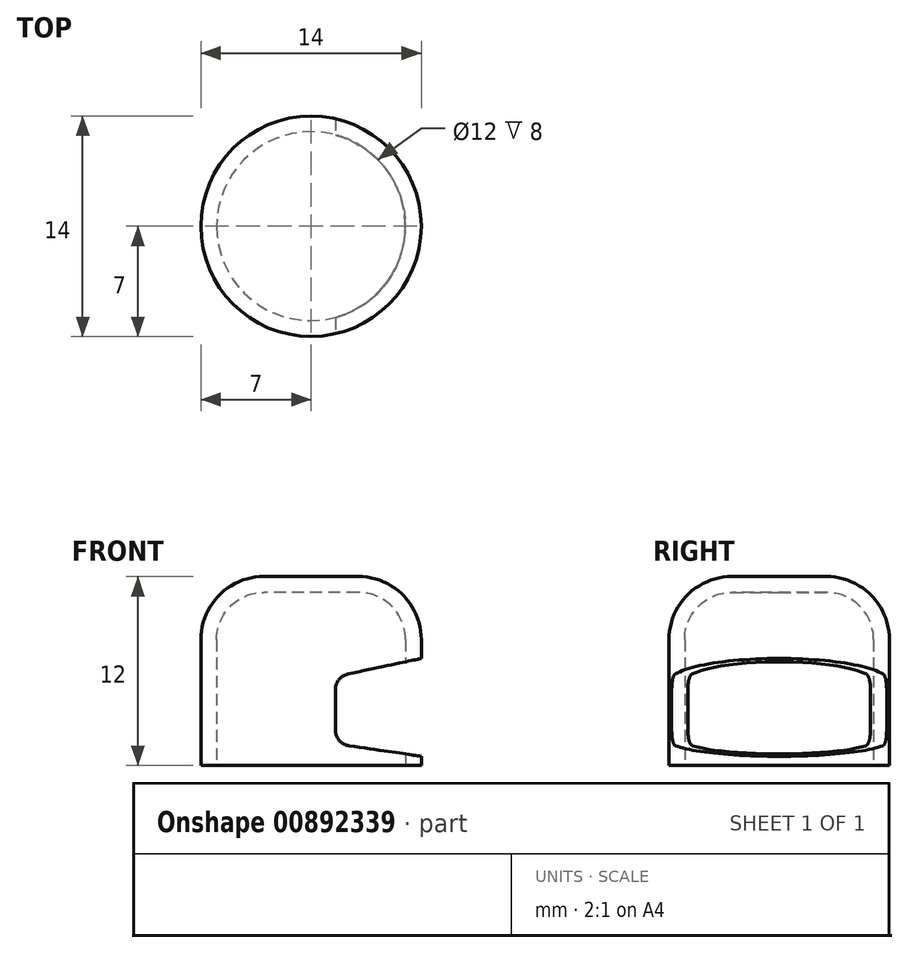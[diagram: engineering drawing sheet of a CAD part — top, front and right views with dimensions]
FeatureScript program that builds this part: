
annotation { "Feature Type Name" : "Feature", "Feature Type Description" : "" }
export const myFeature = defineFeature(function(context is Context, id is Id, definition is map)
    precondition{}
    {
        {
            var Q0;
            Q0=qCreatedBy(makeId("Top.planeOp"),FACE);
            var sketch = newSketch(context, id + "F0", { "sketchPlane" : qUnion([Q0])});
            skCircle(sketch, "E0", {"center": v(0, 0) * mm, "radius": 7 * mm});
            skSolve(sketch);
        }
        {
            var Q0;
            Q0 = qSketchRegion(id + "F0", true);
            extrude(context, id + "F1", {"entities" : qUnion([Q0]), "depth" : 12 * mm, "offsetDistance" : 25.4 * mm});
        }
        {
            var Q0;
            Q0=makeQuery(id+"F1.opExtrude","CAP_FACE",FACE,{"disambiguationData":[OSD([sQuery(id+"F0.wireOp",EDGE,"E0")])],"isStart":false});
            fillet(context, id + "F2", {"entities" : qUnion([Q0]), "radius" : 4 * mm, "tangentPropagation" : true, "allowEdgeOverflow" : false});
        }
        {
            var Q0;
            Q0=makeQuery(id+"F1.opExtrude","CAP_FACE",FACE,{"disambiguationData":[OSD([sQuery(id+"F0.wireOp",EDGE,"E0")])],"isStart":true});
            shell(context, id + "F3", {"entities" : qUnion([Q0]), "thickness" : 1 * mm});
        }
        {
            var Q0;
            Q0=qCreatedBy(makeId("Front.planeOp"),FACE);
            var sketch = newSketch(context, id + "F4", { "sketchPlane" : qUnion([Q0])});
            skLineSegment(sketch, "E1", {"start": v(8.23, 7.06) * mm, "end": v(2.34, 5.8) * mm});
            skLineSegment(sketch, "E2", {"start": v(1.55, 4.83) * mm, "end": v(1.55, 2.24) * mm});
            skLineSegment(sketch, "E3", {"start": v(2.4, 1.25) * mm, "end": v(7.23, 0.55) * mm});
            skLineSegment(sketch, "E4", {"start": v(7.23, 0.55) * mm, "end": v(8.12, 6.7) * mm});
            skLineSegment(sketch, "E5", {"start": v(8.12, 6.7) * mm, "end": v(8.23, 7.06) * mm});
            skPoint(sketch, "E6.visualSharp", {"position": v(1.55, 5.64) * mm});
            skArc(sketch, "E6.filletArc", {"start": v(2.34, 5.8) * mm, "mid": v(1.77, 5.46) * mm, "end": v(1.55, 4.83) * mm});
            skPoint(sketch, "E7.visualSharp", {"position": v(1.55, 1.38) * mm});
            skArc(sketch, "E7.filletArc", {"start": v(1.55, 2.24) * mm, "mid": v(1.79, 1.59) * mm, "end": v(2.4, 1.25) * mm});
            skSolve(sketch);
        }
        {
            var Q0;
            Q0=makeQuery(id+"F4.imprint","IMPRINT",FACE,{"disambiguationData":[TD([[makeQuery(id+"F4.imprint","IMPRINT",EDGE,{"derivedFrom":sQuery(id+"F4.wireOp",EDGE,"E1")}),1.0]])]});
            extrude(context, id + "F5", {"entities" : qUnion([Q0]), "operationType" : NewBodyOperationType.REMOVE, "endBound" : BoundingType.SYMMETRIC, "oppositeDirection" : true, "depth" : 25.4 * mm, "offsetDistance" : 25.4 * mm});
        }
    });
